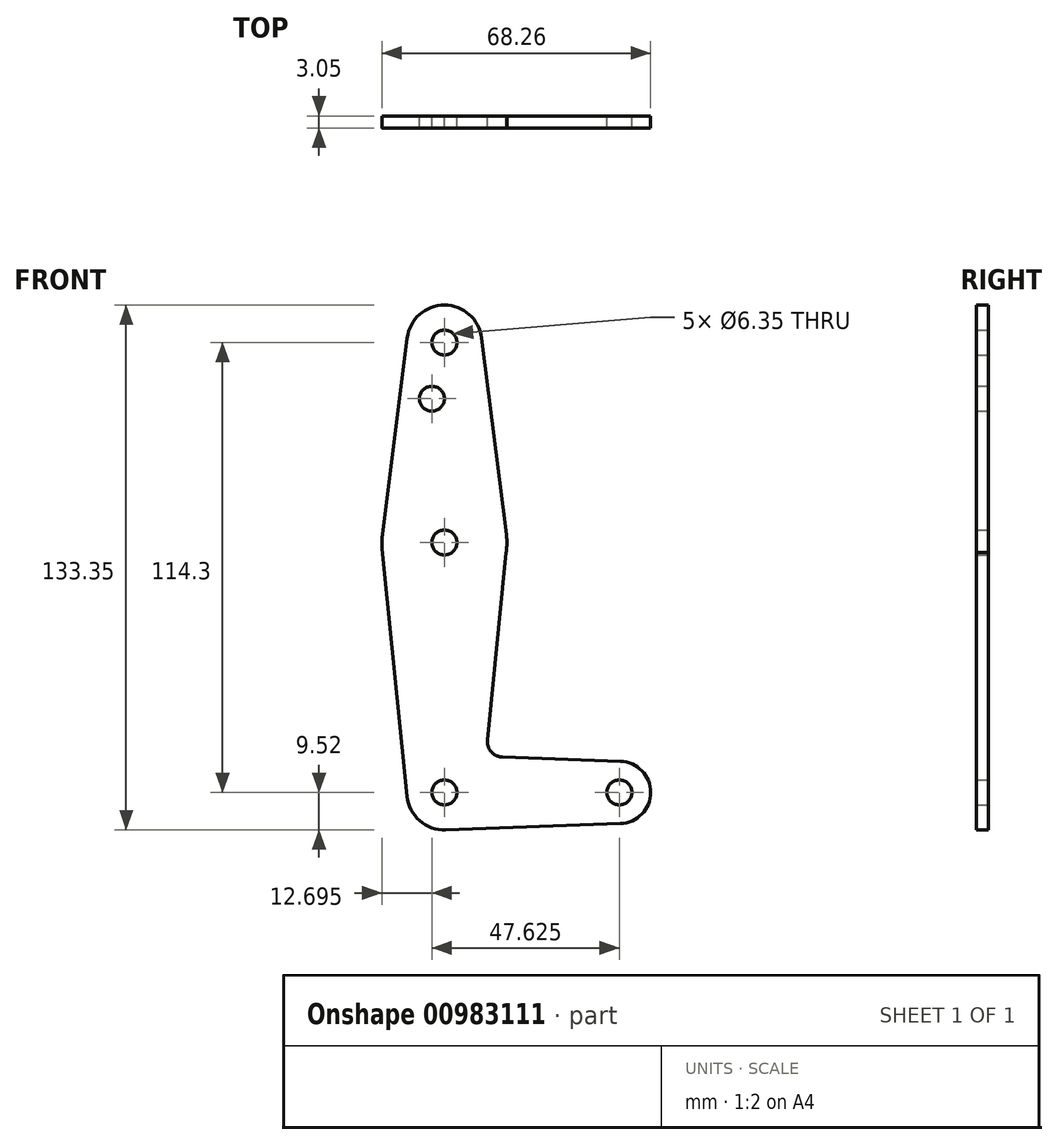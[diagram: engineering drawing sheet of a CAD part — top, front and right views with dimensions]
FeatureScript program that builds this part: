
annotation { "Feature Type Name" : "Feature", "Feature Type Description" : "" }
export const myFeature = defineFeature(function(context is Context, id is Id, definition is map)
    precondition{}
    {
        {
            var Q0;
            Q0=qCreatedBy(makeId("Front.planeOp"),FACE);
            var sketch = newSketch(context, id + "F0", { "sketchPlane" : qUnion([Q0])});
            skLineSegment(sketch, "E0", {"start": v(44.45, 0) * mm, "end": v(0, 0) * mm, "construction": true});
            skLineSegment(sketch, "E1", {"start": v(0, 0) * mm, "end": v(0, 114.3) * mm, "construction": true});
            skCircle(sketch, "E2", {"center": v(0, 0) * mm, "radius": 9.53 * mm});
            skCircle(sketch, "E3", {"center": v(44.45, 0) * mm, "radius": 7.94 * mm});
            skCircle(sketch, "E4", {"center": v(0, 114.3) * mm, "radius": 9.53 * mm});
            skCircle(sketch, "E5", {"center": v(0, 63.5) * mm, "radius": 15.88 * mm});
            skLineSegment(sketch, "E6", {"start": v(-9.45, 115.5) * mm, "end": v(-15.75, 65.48) * mm});
            skCircle(sketch, "E7", {"center": v(0, 114.3) * mm, "radius": 3.18 * mm});
            skCircle(sketch, "E8", {"center": v(0, 63.5) * mm, "radius": 3.18 * mm});
            skCircle(sketch, "E9", {"center": v(0, 0) * mm, "radius": 3.18 * mm});
            skCircle(sketch, "E10", {"center": v(44.45, 0) * mm, "radius": 3.18 * mm});
            skCircle(sketch, "E11", {"center": v(-3.18, 100.03) * mm, "radius": 3.18 * mm});
            skLineSegment(sketch, "E12", {"start": v(0.34, -9.52) * mm, "end": v(44.73, -7.93) * mm});
            skLineSegment(sketch, "E13", {"start": v(9.45, 115.5) * mm, "end": v(15.75, 65.48) * mm});
            skPoint(sketch, "E14.third.point.positionSnap0", {"position": v(20.55, 6.44) * mm});
            skLineSegment(sketch, "E15.trimOffspring", {"start": v(9.57, 0) * mm, "end": v(9.48, -0.95) * mm});
            skPoint(sketch, "E16.start.orphan", {"position": v(-7.37, 6.03) * mm});
            skLineSegment(sketch, "E17", {"start": v(14.73, 9) * mm, "end": v(44.73, 7.93) * mm});
            skArc(sketch, "E18", {"start": v(10.92, 13.37) * mm, "mid": v(11.88, 10.36) * mm, "end": v(14.73, 9) * mm});
            skPoint(sketch, "E18.first.point", {"position": v(11.13, 14.3) * mm});
            skPoint(sketch, "E18.second.point", {"position": v(14.4, 9.03) * mm});
            skPoint(sketch, "E18.third.point", {"position": v(18.77, 13.76) * mm});
            skLineSegment(sketch, "E19", {"start": v(15.67, 60.98) * mm, "end": v(10.92, 13.37) * mm});
            skLineSegment(sketch, "E20", {"start": v(-15.8, 61.91) * mm, "end": v(-9.48, -0.95) * mm});
            skSolve(sketch);
        }
        {
            var Q0;
            Q0 = qSketchRegion(id + "F0", true);
            extrude(context, id + "F1", {"entities" : qUnion([Q0]), "depth" : 3.05 * mm, "offsetDistance" : 25.4 * mm});
        }
    });
